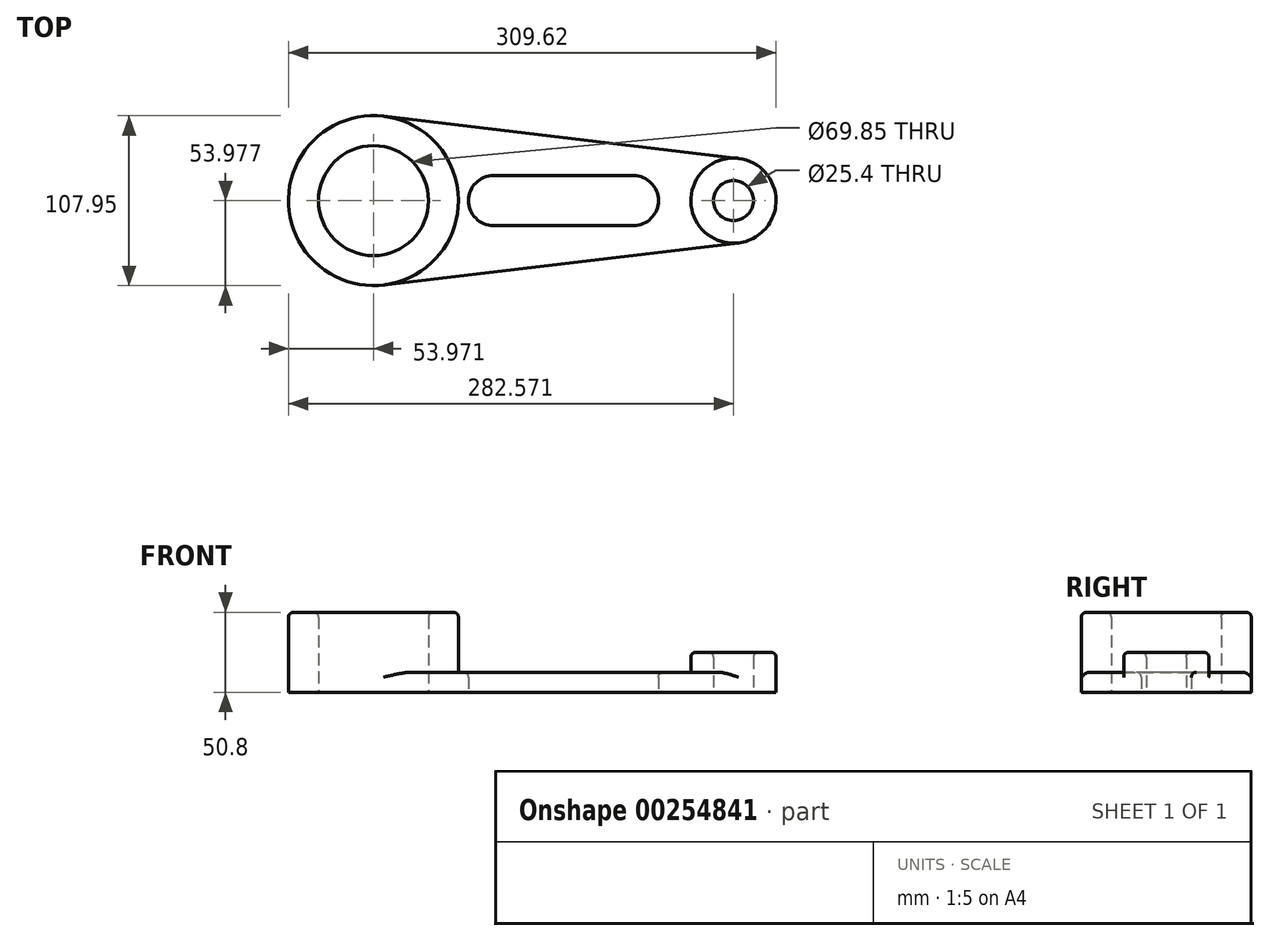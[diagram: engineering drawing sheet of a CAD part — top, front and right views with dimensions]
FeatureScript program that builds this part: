
annotation { "Feature Type Name" : "Feature", "Feature Type Description" : "" }
export const myFeature = defineFeature(function(context is Context, id is Id, definition is map)
    precondition{}
    {
        {
            var Q0;
            Q0=qCreatedBy(makeId("Top.planeOp"),FACE);
            var sketch = newSketch(context, id + "F0", { "sketchPlane" : qUnion([Q0])});
            skCircle(sketch, "E0", {"center": v(-189.4, 7.17) * mm, "radius": 53.98 * mm});
            skCircle(sketch, "E1", {"center": v(-189.4, 7.17) * mm, "radius": 34.93 * mm});
            skCircle(sketch, "E2", {"center": v(39.2, 7.17) * mm, "radius": 12.7 * mm});
            skCircle(sketch, "E3", {"center": v(39.2, 7.17) * mm, "radius": 27.05 * mm});
            skLineSegment(sketch, "E4", {"start": v(-183.04, 60.77) * mm, "end": v(42.39, 34.03) * mm});
            skLineSegment(sketch, "E5", {"start": v(-183.04, -46.43) * mm, "end": v(42.39, -19.7) * mm});
            skArc(sketch, "E6", {"start": v(-113.2, 23.04) * mm, "mid": v(-129.07, 7.17) * mm, "end": v(-113.2, -8.7) * mm});
            skArc(sketch, "E7", {"start": v(-24.3, -8.7) * mm, "mid": v(-8.42, 7.17) * mm, "end": v(-24.3, 23.04) * mm});
            skLineSegment(sketch, "E8", {"start": v(-113.2, 23.04) * mm, "end": v(-24.3, 23.04) * mm});
            skLineSegment(sketch, "E9", {"start": v(-113.2, -8.7) * mm, "end": v(-24.3, -8.7) * mm});
            skSolve(sketch);
        }
        {
            var Q0;
            {var subQ1=sQuery(id+"F0.wireOp",EDGE,"E4");Q0=makeQuery(id+"F0.imprint","IMPRINT",FACE,{"disambiguationData":[TD([[makeQuery(id+"F0.imprint","IMPRINT",EDGE,{"derivedFrom":subQ1}),-1.0]])]});}
            extrude(context, id + "F1", {"entities" : qUnion([Q0]), "depth" : 12.7 * mm});
        }
        {
            var Q0;
            Q0=makeQuery(id+"F0.imprint","IMPRINT",FACE,{"disambiguationData":[TD([[makeQuery(id+"F0.imprint","IMPRINT",EDGE,{"derivedFrom":sQuery(id+"F0.wireOp",EDGE,"E1")}),-1.0]])]});
            extrude(context, id + "F2", {"entities" : qUnion([Q0]), "operationType" : NewBodyOperationType.ADD, "depth" : 50.8 * mm});
        }
        {
            var Q0;
            Q0=makeQuery(id+"F0.imprint","IMPRINT",FACE,{"disambiguationData":[TD([[makeQuery(id+"F0.imprint","IMPRINT",EDGE,{"derivedFrom":sQuery(id+"F0.wireOp",EDGE,"E2")}),-1.0]])]});
            extrude(context, id + "F3", {"entities" : qUnion([Q0]), "operationType" : NewBodyOperationType.ADD, "depth" : 25.4 * mm});
        }
        {
            var Q0;
            Q0=makeQuery(id+"F2.opExtrude","CAP_EDGE",EDGE,{"disambiguationData":[OSD([sQuery(id+"F0.wireOp",EDGE,"E0")])],"isStart":false});
            fillet(context, id + "F4", {"entities" : qUnion([Q0]), "radius" : 3.17 * mm, "tangentPropagation" : true, "allowEdgeOverflow" : false});
        }
        {
            var Q0;
            Q0=makeQuery(id+"F2.opExtrude","CAP_EDGE",EDGE,{"disambiguationData":[OSD([sQuery(id+"F0.wireOp",EDGE,"E1")])],"isStart":false});
            var Q1;
            Q1=makeQuery(id+"F3.opExtrude","CAP_EDGE",EDGE,{"disambiguationData":[OSD([sQuery(id+"F0.wireOp",EDGE,"E2")])],"isStart":false});
            var Q2;
            Q2=makeQuery(id+"F3.opExtrude","CAP_EDGE",EDGE,{"disambiguationData":[OSD([sQuery(id+"F0.wireOp",EDGE,"E3")])],"isStart":false});
            var Q3;
            Q3=makeQuery(id+"F1.opExtrude","CAP_EDGE",EDGE,{"disambiguationData":[OSD([sQuery(id+"F0.wireOp",EDGE,"E4")])],"isStart":false});
            var Q4;
            Q4=makeQuery(id+"F1.opExtrude","CAP_EDGE",EDGE,{"disambiguationData":[OSD([sQuery(id+"F0.wireOp",EDGE,"E5")])],"isStart":false});
            var Q5;
            Q5=makeQuery(id+"F1.opExtrude","CAP_EDGE",EDGE,{"disambiguationData":[OSD([sQuery(id+"F0.wireOp",EDGE,"E9")])],"isStart":false});
            fillet(context, id + "F5", {"entities" : qUnion([Q0, Q1, Q2, Q3, Q4, Q5]), "radius" : 3.17 * mm, "tangentPropagation" : true, "allowEdgeOverflow" : false});
        }
    });
